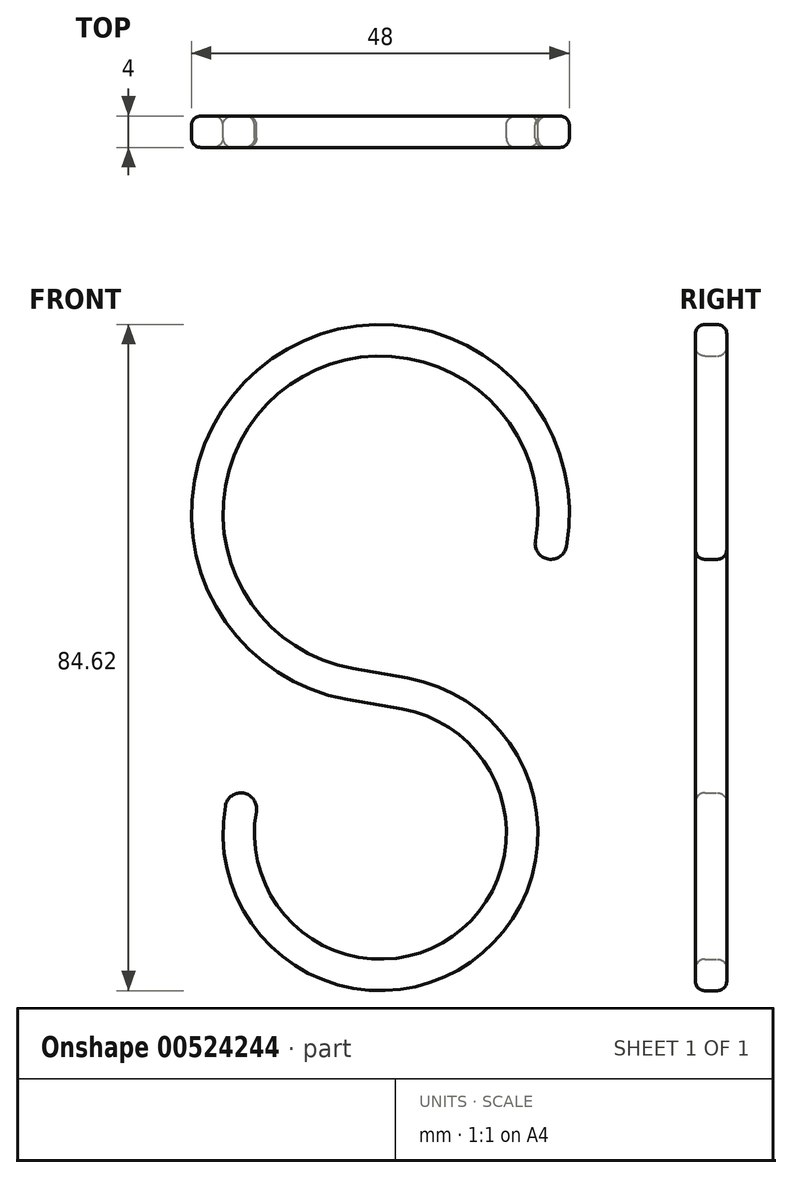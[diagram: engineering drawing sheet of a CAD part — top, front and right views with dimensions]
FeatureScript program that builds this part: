
annotation { "Feature Type Name" : "Feature", "Feature Type Description" : "" }
export const myFeature = defineFeature(function(context is Context, id is Id, definition is map)
    precondition{}
    {
        {
            var Q0;
            Q0=qCreatedBy(makeId("Front.planeOp"),FACE);
            var sketch = newSketch(context, id + "F0", { "sketchPlane" : qUnion([Q0])});
            skArc(sketch, "E0", {"start": v(19.7, -3.47) * mm, "mid": v(-11.47, 16.38) * mm, "end": v(-3.47, -19.7) * mm});
            skArc(sketch, "E1", {"start": v(-19.7, -37.14) * mm, "mid": v(11.47, -57) * mm, "end": v(3.47, -20.92) * mm});
            skLineSegment(sketch, "E2", {"start": v(-3.47, -19.7) * mm, "end": v(3.47, -20.92) * mm});
            skLineSegment(sketch, "E3", {"start": v(0, 0) * mm, "end": v(45.17, -7.96) * mm, "construction": true});
            skLineSegment(sketch, "E4", {"start": v(0, -40.62) * mm, "end": v(-41.8, -33.25) * mm, "construction": true});
            skLineSegment(sketch, "E5", {"start": v(0, -43.92) * mm, "end": v(0, -40.62) * mm, "construction": true});
            skArc(sketch, "E6.0", {"start": v(-15.76, -37.84) * mm, "mid": v(9.18, -53.72) * mm, "end": v(2.78, -24.86) * mm});
            skLineSegment(sketch, "E6.1", {"start": v(-4.17, -23.64) * mm, "end": v(2.78, -24.86) * mm});
            skArc(sketch, "E6.2", {"start": v(23.64, -4.17) * mm, "mid": v(-13.77, 19.66) * mm, "end": v(-4.17, -23.64) * mm});
            skArc(sketch, "E7", {"start": v(19.7, -3.47) * mm, "mid": v(21.32, -5.79) * mm, "end": v(23.64, -4.17) * mm});
            skPoint(sketch, "E7.third.point", {"position": v(21, -5.7) * mm});
            skArc(sketch, "E8", {"start": v(-15.76, -37.84) * mm, "mid": v(-17.38, -35.52) * mm, "end": v(-19.7, -37.14) * mm});
            skPoint(sketch, "E8.third.point", {"position": v(-15.76, -37.84) * mm});
            skSolve(sketch);
        }
        {
            var Q0;
            Q0 = qSketchRegion(id + "F0", true);
            extrude(context, id + "F1", {"entities" : qUnion([Q0]), "depth" : 4 * mm, "offsetDistance" : 25 * mm});
        }
        {
            var Q0;
            Q0=makeQuery(id+"F1.opExtrude","CAP_EDGE",EDGE,{"disambiguationData":[OSD([sQuery(id+"F0.wireOp",EDGE,"E1")])],"isStart":false});
            var Q1;
            Q1=makeQuery(id+"F1.opExtrude","CAP_EDGE",EDGE,{"disambiguationData":[OSD([sQuery(id+"F0.wireOp",EDGE,"E1")])],"isStart":true});
            fillet(context, id + "F2", {"entities" : qUnion([Q0, Q1]), "radius" : 1.2 * mm, "tangentPropagation" : true, "defaultsChanged" : true, "vertexSettings" : [], "allowEdgeOverflow" : false});
        }
    });
